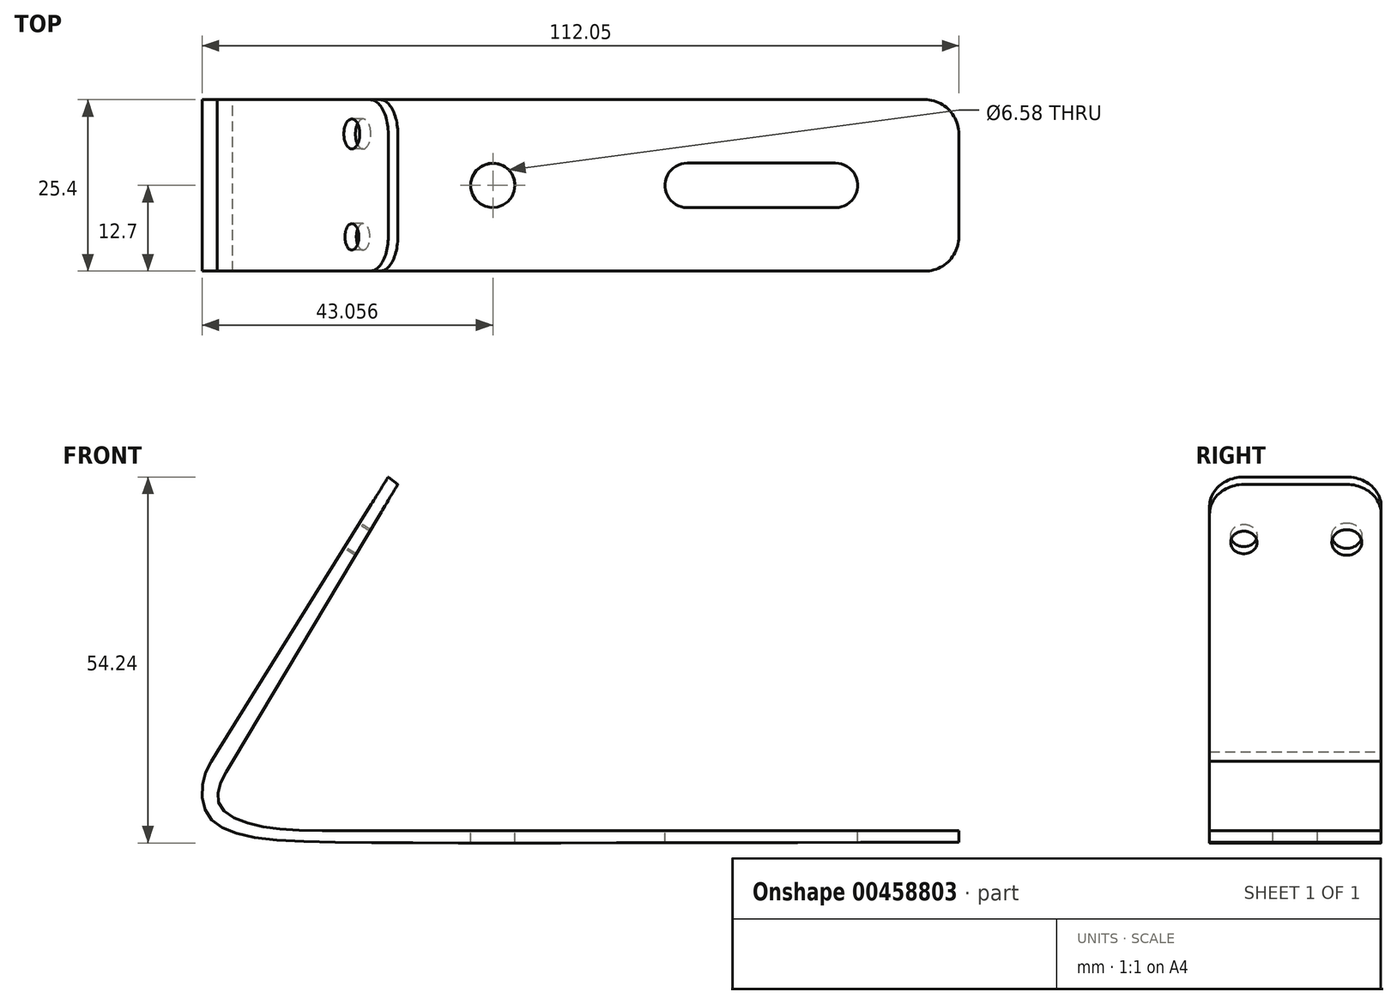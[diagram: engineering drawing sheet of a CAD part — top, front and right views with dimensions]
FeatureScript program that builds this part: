
annotation { "Feature Type Name" : "Feature", "Feature Type Description" : "" }
export const myFeature = defineFeature(function(context is Context, id is Id, definition is map)
    precondition{}
    {
        {
            var Q0;
            Q0=qCreatedBy(makeId("Front.planeOp"),FACE);
            var sketch = newSketch(context, id + "F0", { "sketchPlane" : qUnion([Q0])});
            skLineSegment(sketch, "E0", {"start": v(49.15, -1.73) * mm, "end": v(49.15, 0) * mm});
            skLineSegment(sketch, "E1", {"start": v(-33.91, 51.31) * mm, "end": v(-35.33, 52.4) * mm});
            skFitSpline(sketch, "E2", {"points": [v(49.15, -1.73) * mm, v(-40.68, -1.73) * mm, v(-58.96, 0) * mm, v(-62.47, 3.21) * mm, v(-62.58, 7.93) * mm, v(-60.62, 11.7) * mm], "startDerivative": vector(-223.66, 0) * mm, "endDerivative": vector(22.74, 34.42) * mm});
            skLineSegment(sketch, "E3", {"start": v(-60.62, 11.7) * mm, "end": v(-35.33, 52.4) * mm});
            skFitSpline(sketch, "E4", {"points": [v(49.15, 0) * mm, v(-40.53, 0) * mm, v(-55.07, 0.85) * mm, v(-60.04, 3.35) * mm, v(-60.42, 6.23) * mm, v(-58.36, 10.28) * mm], "startDerivative": vector(-222.85, -0.05) * mm, "endDerivative": vector(23.44, 37.65) * mm});
            skLineSegment(sketch, "E5", {"start": v(-58.36, 10.28) * mm, "end": v(-33.91, 51.31) * mm});
            skSolve(sketch);
        }
        {
            var Q0;
            Q0=makeQuery(id+"F0.imprint","IMPRINT",FACE,{"disambiguationData":[TD([[makeQuery(id+"F0.imprint","IMPRINT",EDGE,{"derivedFrom":sQuery(id+"F0.wireOp",EDGE,"E0")}),1.0]])]});
            extrude(context, id + "F1", {"entities" : qUnion([Q0]), "depth" : 25.4 * mm, "offsetDistance" : 25.4 * mm, "symmetric" : true});
        }
        {
            var Q0;
            Q0=qCreatedBy(makeId("Top.planeOp"),FACE);
            var sketch = newSketch(context, id + "F2", { "sketchPlane" : qUnion([Q0])});
            skCircle(sketch, "E6", {"center": v(-19.84, 0) * mm, "radius": 3.3 * mm});
            skCircle(sketch, "E7", {"center": v(8.92, 0) * mm, "radius": 3.3 * mm});
            skCircle(sketch, "E8", {"center": v(30.89, 0) * mm, "radius": 3.3 * mm});
            skLineSegment(sketch, "E9", {"start": v(8.92, -3.3) * mm, "end": v(30.89, -3.3) * mm});
            skLineSegment(sketch, "E10", {"start": v(8.92, 3.3) * mm, "end": v(30.89, 3.3) * mm});
            skSolve(sketch);
        }
        {
            var Q0;
            Q0 = qSketchRegion(id + "F2", true);
            extrude(context, id + "F3", {"entities" : qUnion([Q0]), "operationType" : NewBodyOperationType.REMOVE, "oppositeDirection" : true, "depth" : 25.4 * mm, "offsetDistance" : 25.4 * mm});
        }
        {
            var Q0;
            Q0=makeQuery(id+"F1.opExtrude","CAP_EDGE",EDGE,{"disambiguationData":[OSD([sQuery(id+"F0.wireOp",EDGE,"E1")])],"isStart":false});
            var Q1;
            Q1=makeQuery(id+"F1.opExtrude","CAP_EDGE",EDGE,{"disambiguationData":[OSD([sQuery(id+"F0.wireOp",EDGE,"E1")])],"isStart":true});
            var Q2;
            Q2=makeQuery(id+"F1.opExtrude","CAP_EDGE",EDGE,{"disambiguationData":[OSD([sQuery(id+"F0.wireOp",EDGE,"E0")])],"isStart":true});
            var Q3;
            Q3=makeQuery(id+"F1.opExtrude","CAP_EDGE",EDGE,{"disambiguationData":[OSD([sQuery(id+"F0.wireOp",EDGE,"E0")])],"isStart":false});
            fillet(context, id + "F4", {"entities" : qUnion([Q0, Q1, Q2, Q3]), "radius" : 5.08 * mm, "tangentPropagation" : true, "allowEdgeOverflow" : false});
        }
        {
            var Q0;
            Q0=makeQuery(id+"F1.opExtrude","SWEPT_FACE",FACE,{"disambiguationData":[OSD([sQuery(id+"F0.wireOp",EDGE,"E3")])]});
            var sketch = newSketch(context, id + "F5", { "sketchPlane" : qUnion([Q0])});
            skCircle(sketch, "E11", {"center": v(-7.62, 15.66) * mm, "radius": 2.22 * mm});
            skCircle(sketch, "E12", {"center": v(7.62, 15.66) * mm, "radius": 1.96 * mm});
            skSolve(sketch);
        }
        {
            var Q0;
            Q0=makeQuery(id+"F5.imprint","IMPRINT",FACE,{"disambiguationData":[TD([[makeQuery(id+"F5.imprint","IMPRINT",EDGE,{"derivedFrom":sQuery(id+"F5.wireOp",EDGE,"E11")}),1.0]])]});
            var Q1;
            Q1=makeQuery(id+"F5.imprint","IMPRINT",FACE,{"disambiguationData":[TD([[makeQuery(id+"F5.imprint","IMPRINT",EDGE,{"derivedFrom":sQuery(id+"F5.wireOp",EDGE,"E12")}),1.0]])]});
            extrude(context, id + "F6", {"entities" : qUnion([Q0, Q1]), "operationType" : NewBodyOperationType.REMOVE, "oppositeDirection" : true, "depth" : 25.4 * mm, "offsetDistance" : 25.4 * mm});
        }
    });
